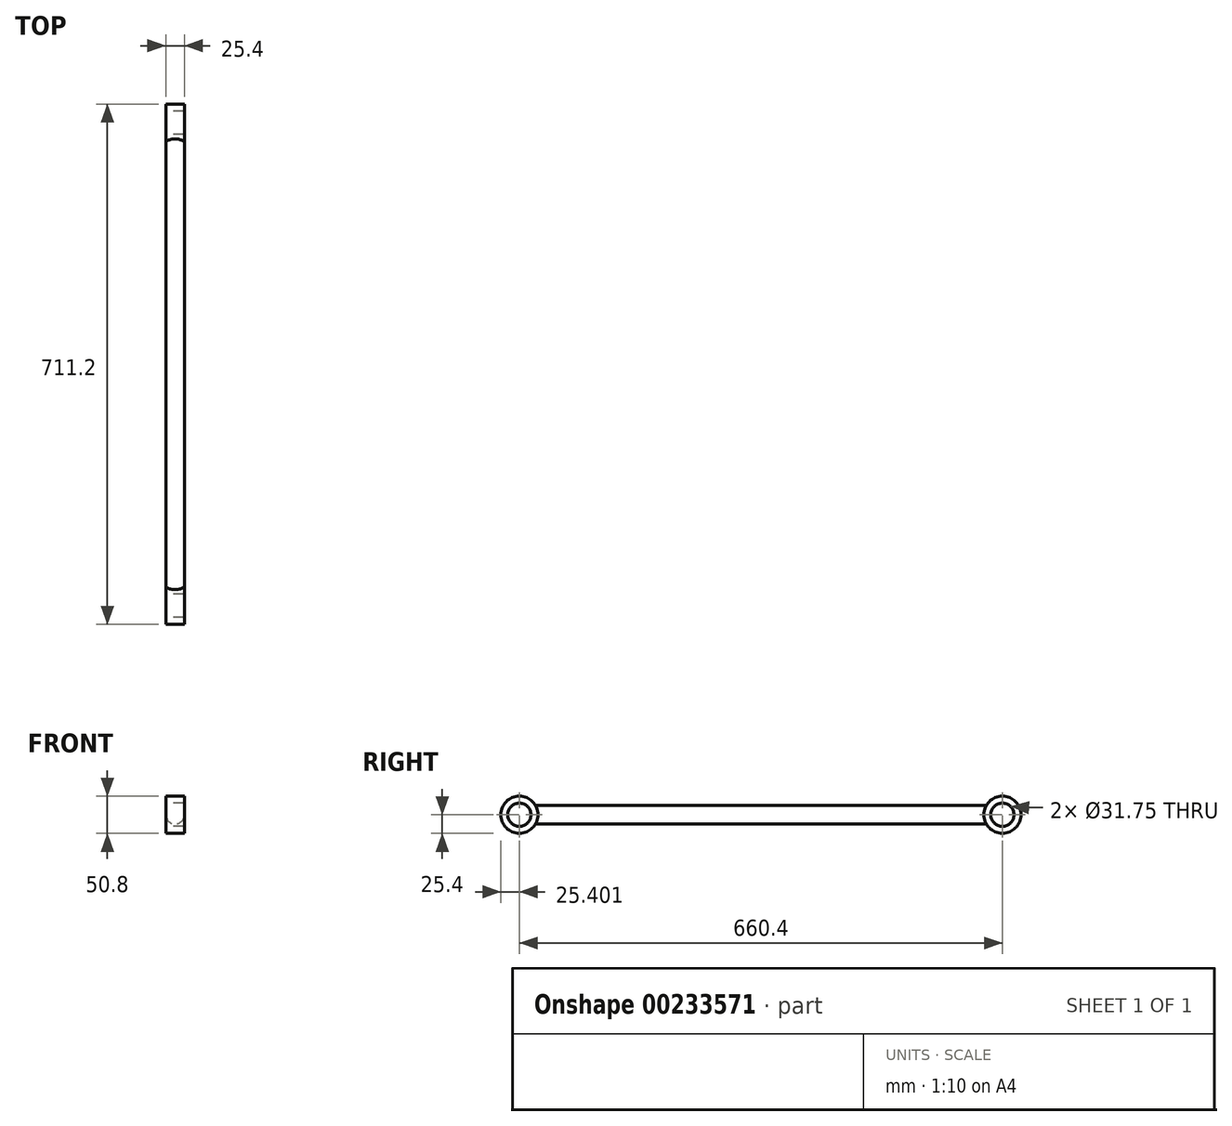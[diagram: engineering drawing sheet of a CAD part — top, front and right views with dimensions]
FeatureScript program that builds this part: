
annotation { "Feature Type Name" : "Feature", "Feature Type Description" : "" }
export const myFeature = defineFeature(function(context is Context, id is Id, definition is map)
    precondition{}
    {
        {
            var Q0;
            Q0=qCreatedBy(makeId("Right.planeOp"),FACE);
            var sketch = newSketch(context, id + "F0", { "sketchPlane" : qUnion([Q0])});
            skCircle(sketch, "E0", {"center": v(-63.6, 0) * mm, "radius": 15.88 * mm});
            skCircle(sketch, "E1", {"center": v(-63.6, 0) * mm, "radius": 25.4 * mm});
            skLineSegment(sketch, "E2", {"start": v(-63.6, 0) * mm, "end": v(596.8, 0) * mm, "construction": true});
            skCircle(sketch, "E3", {"center": v(596.8, 0) * mm, "radius": 15.88 * mm});
            skCircle(sketch, "E4", {"center": v(596.8, 0) * mm, "radius": 25.4 * mm});
            skSolve(sketch);
        }
        {
            var Q0;
            Q0=qCreatedBy(makeId("Front.planeOp"),FACE);
            var sketch = newSketch(context, id + "F1", { "sketchPlane" : qUnion([Q0])});
            skCircle(sketch, "E5", {"center": v(0, 0) * mm, "radius": 12.7 * mm});
            skSolve(sketch);
        }
        {
            var Q0;
            Q0=makeQuery(id+"F0.imprint","IMPRINT",FACE,{"disambiguationData":[TD([[makeQuery(id+"F0.imprint","IMPRINT",EDGE,{"derivedFrom":sQuery(id+"F0.wireOp",EDGE,"E0")}),-1.0]])]});
            extrude(context, id + "F2", {"entities" : qUnion([Q0]), "endBound" : BoundingType.SYMMETRIC, "depth" : 25.4 * mm});
        }
        {
            var Q0;
            Q0=makeQuery(id+"F0.imprint","IMPRINT",FACE,{"disambiguationData":[TD([[makeQuery(id+"F0.imprint","IMPRINT",EDGE,{"derivedFrom":sQuery(id+"F0.wireOp",EDGE,"E3")}),-1.0]])]});
            extrude(context, id + "F3", {"entities" : qUnion([Q0]), "endBound" : BoundingType.SYMMETRIC, "depth" : 25.4 * mm});
        }
        {
            var Q0;
            Q0=makeQuery(id+"F1.imprint","IMPRINT",FACE,{"disambiguationData":[TD([[makeQuery(id+"F1.imprint","IMPRINT",EDGE,{"derivedFrom":sQuery(id+"F1.wireOp",EDGE,"E5")}),1.0]])]});
            var Q1;
            Q1=makeQuery(id+"F2.opExtrude","SWEPT_FACE",FACE,{"disambiguationData":[OSD([sQuery(id+"F0.wireOp",EDGE,"E1")])]});
            var Q2;
            Q2=makeQuery(id+"F3.opExtrude","SWEPT_FACE",FACE,{"disambiguationData":[OSD([sQuery(id+"F0.wireOp",EDGE,"E4")])]});
            extrude(context, id + "F4", {"entities" : qUnion([Q0]), "operationType" : NewBodyOperationType.ADD, "endBound" : BoundingType.UP_TO_SURFACE, "endBoundEntityFace" : qUnion([Q1]), "depth" : 25.4 * mm, "hasSecondDirection" : true, "secondDirectionBound" : SecondDirectionBoundingType.UP_TO_SURFACE, "secondDirectionOppositeDirection" : true, "secondDirectionBoundEntityFace" : qUnion([Q2]), "secondDirectionDepth" : 25.4 * mm});
        }
    });
